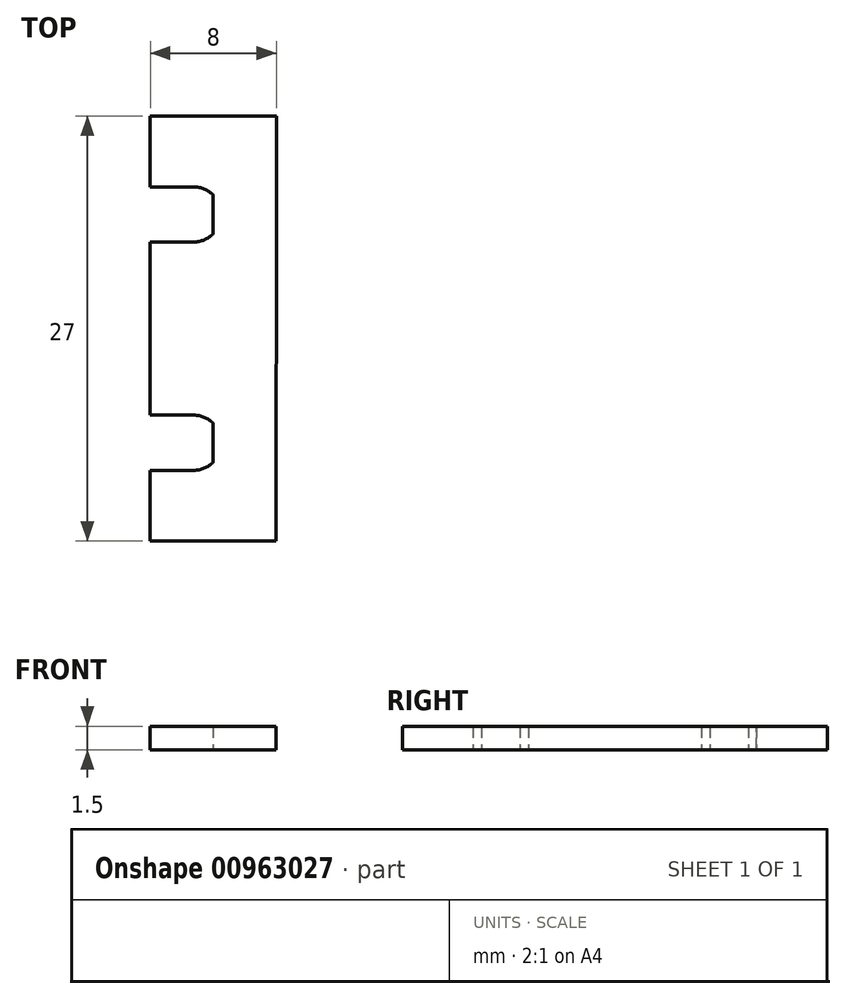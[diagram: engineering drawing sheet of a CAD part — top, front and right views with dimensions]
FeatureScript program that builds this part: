
annotation { "Feature Type Name" : "Feature", "Feature Type Description" : "" }
export const myFeature = defineFeature(function(context is Context, id is Id, definition is map)
    precondition{}
    {
        {
            var Q0;
            Q0=qCreatedBy(makeId("Top.planeOp"),FACE);
            var sketch = newSketch(context, id + "F0", { "sketchPlane" : qUnion([Q0])});
            skLineSegment(sketch, "E0.bottom", {"start": v(-34.62, -35.05) * mm, "end": v(-26.62, -35.05) * mm});
            skLineSegment(sketch, "E0.top", {"start": v(-34.62, -57.55) * mm, "end": v(-26.62, -57.55) * mm});
            skLineSegment(sketch, "E0.right", {"start": v(-26.62, -35.05) * mm, "end": v(-26.62, -57.55) * mm});
            skLineSegment(sketch, "E1", {"start": v(-34.62, -35.05) * mm, "end": v(-34.62, -35.05) * mm});
            skLineSegment(sketch, "E2", {"start": v(-34.62, -57.55) * mm, "end": v(-34.62, -53.05) * mm});
            skLineSegment(sketch, "E3", {"start": v(-34.62, -53.05) * mm, "end": v(-26.62, -53.05) * mm});
            skLineSegment(sketch, "E4", {"start": v(-26.62, -49.55) * mm, "end": v(-34.62, -49.55) * mm});
            skLineSegment(sketch, "E5", {"start": v(-34.62, -49.55) * mm, "end": v(-34.62, -38.55) * mm});
            skLineSegment(sketch, "E6", {"start": v(-34.62, -38.55) * mm, "end": v(-26.62, -38.55) * mm});
            skLineSegment(sketch, "E7", {"start": v(-30.62, -35.05) * mm, "end": v(-30.62, -53.05) * mm});
            skArc(sketch, "E8", {"start": v(-31.87, -38.55) * mm, "mid": v(-30.12, -36.8) * mm, "end": v(-31.87, -35.05) * mm});
            skPoint(sketch, "E9", {"position": v(-30.62, -38.55) * mm});
            skPoint(sketch, "E10", {"position": v(-30.62, -30.55) * mm});
            skArc(sketch, "E11", {"start": v(-31.87, -53.05) * mm, "mid": v(-30.12, -51.3) * mm, "end": v(-31.87, -49.55) * mm});
            skPoint(sketch, "E12", {"position": v(-30.62, -51.3) * mm});
            skLineSegment(sketch, "E13.bottom", {"start": v(-30.62, -30.55) * mm, "end": v(-26.62, -30.55) * mm});
            skLineSegment(sketch, "E13.right", {"start": v(-26.62, -30.55) * mm, "end": v(-26.62, -35.05) * mm});
            skLineSegment(sketch, "E14.bottom", {"start": v(-30.62, -30.55) * mm, "end": v(-34.62, -30.55) * mm});
            skLineSegment(sketch, "E14.top", {"start": v(-30.62, -35.05) * mm, "end": v(-34.62, -35.05) * mm});
            skLineSegment(sketch, "E14.right", {"start": v(-34.62, -30.55) * mm, "end": v(-34.62, -35.05) * mm});
            skSolve(sketch);
        }
        {
            var Q0;
            Q0 = qSketchRegion(id + "F0", true);
            extrude(context, id + "F1", {"entities" : qUnion([Q0]), "depth" : 1.5 * mm, "offsetDistance" : 25.4 * mm});
        }
    });
